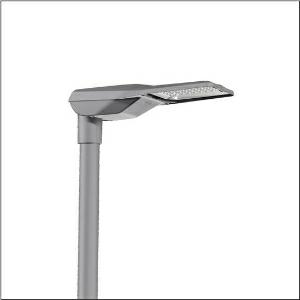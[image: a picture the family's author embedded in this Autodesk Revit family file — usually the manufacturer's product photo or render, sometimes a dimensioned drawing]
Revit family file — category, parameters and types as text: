
# Revit family: streetlight_sl_21_iq_mini___stw1_0a_5xe2e31d08gb_aef3
name_source: partatom
category: Lighting Fixtures
units: mm (PartAtom-declared; Revit-internal decimal feet)

## family parameters
Cut with Voids When Loaded = No
Host = Face
Light Source = No
Part Type = Normal
Room Calculation Point = No
Round Connector Dimension = Use Diameter
Shared = No

## types (1)
- --- (1 x LED, 5680 lm, 37.1 W, 3000K)
    Apparent Load = 37 VA
    CIE Flux Codes = 38 75 98 100 100
    Color Rendering = 70
    Color Temperature = 3000K
    Default Elevation = 1800 mm
    Description = Streetlight SL 21 mini, mast luminaire, primary light control with lens, of PMMA, primary optical cover: cover, of toughened safety glass, transparent, light distribution: STW1.0a, light emission: direct distribution, primary light characteristic: asymmetric, installation type: post-top, side-entry, LED, High Power LED, rated luminous flux: 5.680lm, luminous efficacy: 153lm/W, light colour: 730, colour temperature: 3000K, control gear: ECG iQ, control: Auto-Match, Temp-Guard, Lumen-Switch, Night-Set, Smart-Wire, Light-Fading, Desk-Remote (wireless, voltage-free reading and setting of iQ features in the workshop via application-optimized NFC function/RFID function), optimised constant luminous flux control (CLO 2.0), mains connection: 220..240V, AC, 50/60Hz, start of lifetime: 37W, end of lifetime: 39W, reduction: 18W, luminaire housing, of diecast aluminium, powder-coated, Siteco® metallic grey (DB 702S), corrosivity category C5 according to DIN EN ISO 12944, length: 628mm, width: 235mm, height: 110mm, spigot size: 60/76mm (post-top) and 42/60/76mm (side-entry), mast flange for spigot size: 42mm: 5XC10008XM4, 60mm: 5XC10008XM2, 76/60mm: 5XC10108XM1, protection rating (complete): IP66, insulation class (complete): insulation class II (safety insulation), certification: CE, ENEC, VDE, impact resistance: IK09, permissible operating ambient temperature for outdoor applications: -40..+50°C, standard-compliant lighting for roads and squares, packaging unit: 1 piece

Light Distribution: STW1.0a
    Height = 110 mm
    Lamp = 1 x LED
    Lamp Light Flux = 5680 lm
    Lamp Power = 37.1 W
    Lamp count = 1
    Length = 625 mm
    Luminous efficacy = 153 lm/W
    Manufacturer = Siteco
    ModVariant = No
    Model = 5XE2E31D08GB
    Number of Poles = 1
    OnlyDefault = Yes
    Power Factor = 1
    Product Name = Streetlight SL 21 iQ mini | STW1.0a
    Product group = mast luminaire | pylon top
    ProductGroupID = 6100
    Protection Class = Protection class II
    Protection Degree = IP 66
    RLX_Detail_Level = 1
    RlxData = <blob elided: 91997 chars, md5=d2f526e5>
    Socket = socket
    Standby Power = 0 W
    System Light Flux = 5680 lm
    System Power = 37 W
    Type Comments = factory setting: luminous flux: 100 % | dim-lin: 254 | 385 mA
    Type Image = l_1003519.jpg
    URL = http://relux.com
    VarID = @adj_104965
    Voltage = 0 V
    Weight = 0.00 kg
    Width = 234 mm

## geometry (parser evidence)
native form markers: Blend x4, Sweep x11
no freeform markers — native parametric forms only
